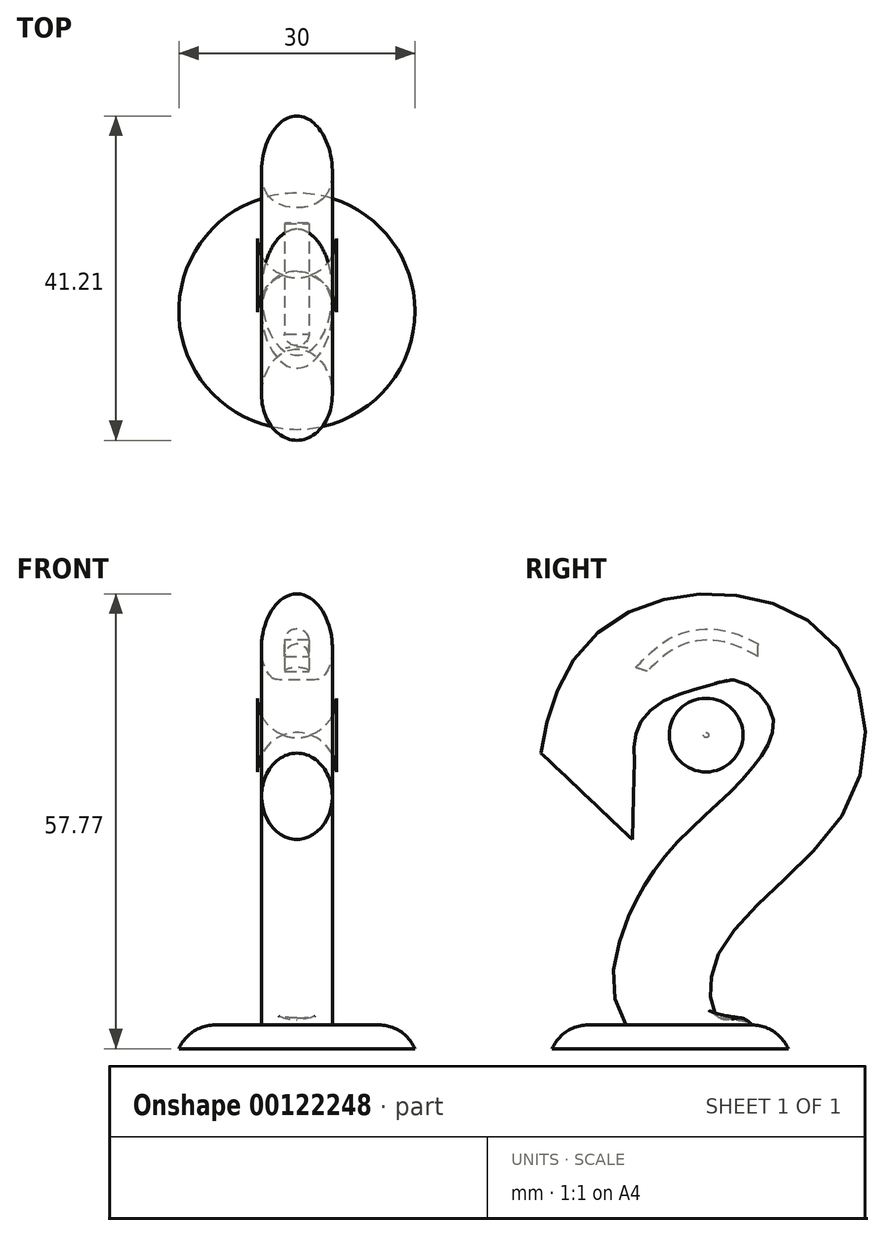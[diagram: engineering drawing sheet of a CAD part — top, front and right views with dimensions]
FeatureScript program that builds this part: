
annotation { "Feature Type Name" : "Feature", "Feature Type Description" : "" }
export const myFeature = defineFeature(function(context is Context, id is Id, definition is map)
    precondition{}
    {
        {
            var Q0;
            Q0=qCreatedBy(makeId("Top.planeOp"),FACE);
            var sketch = newSketch(context, id + "F0", { "sketchPlane" : qUnion([Q0])});
            skCircle(sketch, "E0", {"center": v(0, 0) * mm, "radius": 15 * mm});
            skSolve(sketch);
        }
        {
            var Q0;
            Q0=makeQuery(id+"F0.imprint","IMPRINT",FACE,{"disambiguationData":[TD([[makeQuery(id+"F0.imprint","IMPRINT",EDGE,{"derivedFrom":sQuery(id+"F0.wireOp",EDGE,"E0")}),1.0]])]});
            extrude(context, id + "F1", {"entities" : qUnion([Q0]), "depth" : 3 * mm});
        }
        {
            var Q0;
            Q0=makeQuery(id+"F1.opExtrude","CAP_EDGE",EDGE,{"disambiguationData":[OSD([sQuery(id+"F0.wireOp",EDGE,"E0")])],"isStart":false});
            fillet(context, id + "F2", {"entities" : qUnion([Q0]), "radius" : 5 * mm, "tangentPropagation" : true, "allowEdgeOverflow" : false});
        }
        {
            var Q0;
            Q0=makeQuery(id+"F1.opExtrude","CAP_FACE",FACE,{"disambiguationData":[OSD([sQuery(id+"F0.wireOp",EDGE,"E0")])],"isStart":false});
            var sketch = newSketch(context, id + "F3", { "sketchPlane" : qUnion([Q0])});
            skEllipse(sketch, "E1", {"center": v(0, 2.42) * mm, "majorRadius": 8 * mm, "minorRadius": 4.5 * mm, "majorAxis": v(0, 1)});
            skLineSegment(sketch, "E2", {"start": v(0, 2.42) * mm, "end": v(10.13, 2.42) * mm, "construction": true});
            skLineSegment(sketch, "E3", {"start": v(0, 10.42) * mm, "end": v(0, -5.58) * mm, "construction": true});
            skPoint(sketch, "E3.startSnap0", {"position": v(0, -5.58) * mm});
            skPoint(sketch, "E4", {"position": v(0, 10.42) * mm});
            skSolve(sketch);
        }
        {
            var Q0;
            Q0=makeQuery(id+"F3.imprint","IMPRINT",FACE,{"disambiguationData":[TD([[makeQuery(id+"F3.imprint","IMPRINT",EDGE,{"derivedFrom":sQuery(id+"F3.wireOp",EDGE,"E1")}),1.0]])]});
            var Q1;
            Q1=sQuery(id+"F3.wireOp",EDGE,"E3");
            cPlane(context, id + "F4", {"entities" : qUnion([Q0, Q1]), "cplaneType" : CPlaneType.LINE_ANGLE, "offset" : 25 * mm, "angle" : 90 * degree, "width" : 150 * mm, "height" : 150 * mm});
        }
        {
            var Q0;
            Q0=qCreatedBy(id+"F4.planeOp",FACE);
            var sketch = newSketch(context, id + "F5", { "sketchPlane" : qUnion([Q0])});
            skLineSegment(sketch, "E5", {"start": v(2.42, 3) * mm, "end": v(2.42, 53) * mm, "construction": true});
            skFitSpline(sketch, "E6", {"points": [v(2.42, 3) * mm, v(0, 7.77) * mm, v(3.82, 19.27) * mm, v(17.01, 35.34) * mm, v(14.63, 47.8) * mm, v(2.42, 50.76) * mm, v(-6.9, 45.2) * mm, v(-10.6, 32.05) * mm], "startDerivative": vector(-37.44, 47.18) * mm, "endDerivative": vector(-8.25, -95.5) * mm});
            skSolve(sketch);
        }
        {
            var Q0;
            Q0=makeQuery(id+"F3.imprint","IMPRINT",FACE,{"disambiguationData":[TD([[makeQuery(id+"F3.imprint","IMPRINT",EDGE,{"derivedFrom":sQuery(id+"F3.wireOp",EDGE,"E1")}),1.0]])]});
            var Q1;
            Q1=sQuery(id+"F5.wireOp",EDGE,"E6");
            sweep(context, id + "F6", {"profiles" : qUnion([Q0]), "path" : qUnion([Q1])});
        }
        {
            var Q0;
            Q0=qCreatedBy(id+"F4.planeOp",FACE);
            cPlane(context, id + "F7", {"entities" : qUnion([Q0]), "cplaneType" : CPlaneType.OFFSET, "offset" : 25 * mm, "width" : 150 * mm, "height" : 150 * mm});
        }
        {
            var Q0;
            Q0=qCreatedBy(id+"F7.planeOp",FACE);
            var sketch = newSketch(context, id + "F8", { "sketchPlane" : qUnion([Q0])});
            skCircle(sketch, "E7", {"center": v(4.57, 39.84) * mm, "radius": 9.68 * mm});
            skSolve(sketch);
        }
        {
            var Q0;
            Q0 = qSketchRegion(id + "F8", true);
            extrude(context, id + "F9", {"entities" : qUnion([Q0]), "depth" : 5 * mm, "hasSecondDirection" : true, "secondDirectionOppositeDirection" : true, "secondDirectionDepth" : 5 * mm});
        }
        {
            var Q0;
            Q0=makeQuery(id+"F9.opExtrude","SWEPT_BODY",BODY,{"disambiguationData":[OSD([sQuery(id+"F8.wireOp",EDGE,"E7")])]});
            transform(context, id + "F10", {"entities" : qUnion([Q0]), "transformType" : TransformType.TRANSLATION_3D, "dx" : -25 * mm, "dy" : 0 * mm, "dz" : 0 * mm, "makeCopy" : false});
        }
        {
            var Q0;
            Q0=makeQuery(id+"F9.opExtrude","CAP_EDGE",EDGE,{"disambiguationData":[OSD([sQuery(id+"F8.wireOp",EDGE,"E7")])],"isStart":false});
            var Q1;
            Q1=makeQuery(id+"F9.opExtrude","CAP_EDGE",EDGE,{"disambiguationData":[OSD([sQuery(id+"F8.wireOp",EDGE,"E7")])],"isStart":true});
            fillet(context, id + "F11", {"entities" : qUnion([Q0, Q1]), "radius" : 5 * mm, "tangentPropagation" : true, "allowEdgeOverflow" : false});
        }
        {
            var Q0;
            Q0=qCreatedBy(id+"F4.planeOp",FACE);
            var sketch = newSketch(context, id + "F12", { "sketchPlane" : qUnion([Q0])});
            skFitSpline(sketch, "E8", {"points": [v(-2.92, 47.94) * mm, v(1.13, 51.14) * mm, v(6.46, 51.78) * mm, v(11.15, 49.86) * mm], "startDerivative": vector(11.16, 11.16) * mm, "endDerivative": vector(13.63, -7.35) * mm});
            skSolve(sketch);
        }
        {
            var Q0;
            Q0=qCreatedBy(makeId("Front.planeOp"),FACE);
            cPlane(context, id + "F13", {"entities" : qUnion([Q0]), "cplaneType" : CPlaneType.OFFSET, "offset" : 10 * mm, "oppositeDirection" : true, "width" : 150 * mm, "height" : 150 * mm});
        }
        {
            var Q0;
            Q0=qCreatedBy(id+"F13.planeOp",FACE);
            var sketch = newSketch(context, id + "F14", { "sketchPlane" : qUnion([Q0])});
            skArc(sketch, "E9", {"start": v(1.56, 50.45) * mm, "mid": v(0, 52) * mm, "end": v(-1.56, 50.45) * mm});
            skLineSegment(sketch, "E10", {"start": v(-1.56, 50.45) * mm, "end": v(1.56, 50.45) * mm});
            skSolve(sketch);
        }
        {
            var Q0;
            Q0 = qSketchRegion(id + "F14", true);
            var Q1;
            Q1=sQuery(id+"F12.wireOp",EDGE,"E8");
            sweep(context, id + "F15", {"profiles" : qUnion([Q0]), "path" : qUnion([Q1])});
        }
    });
